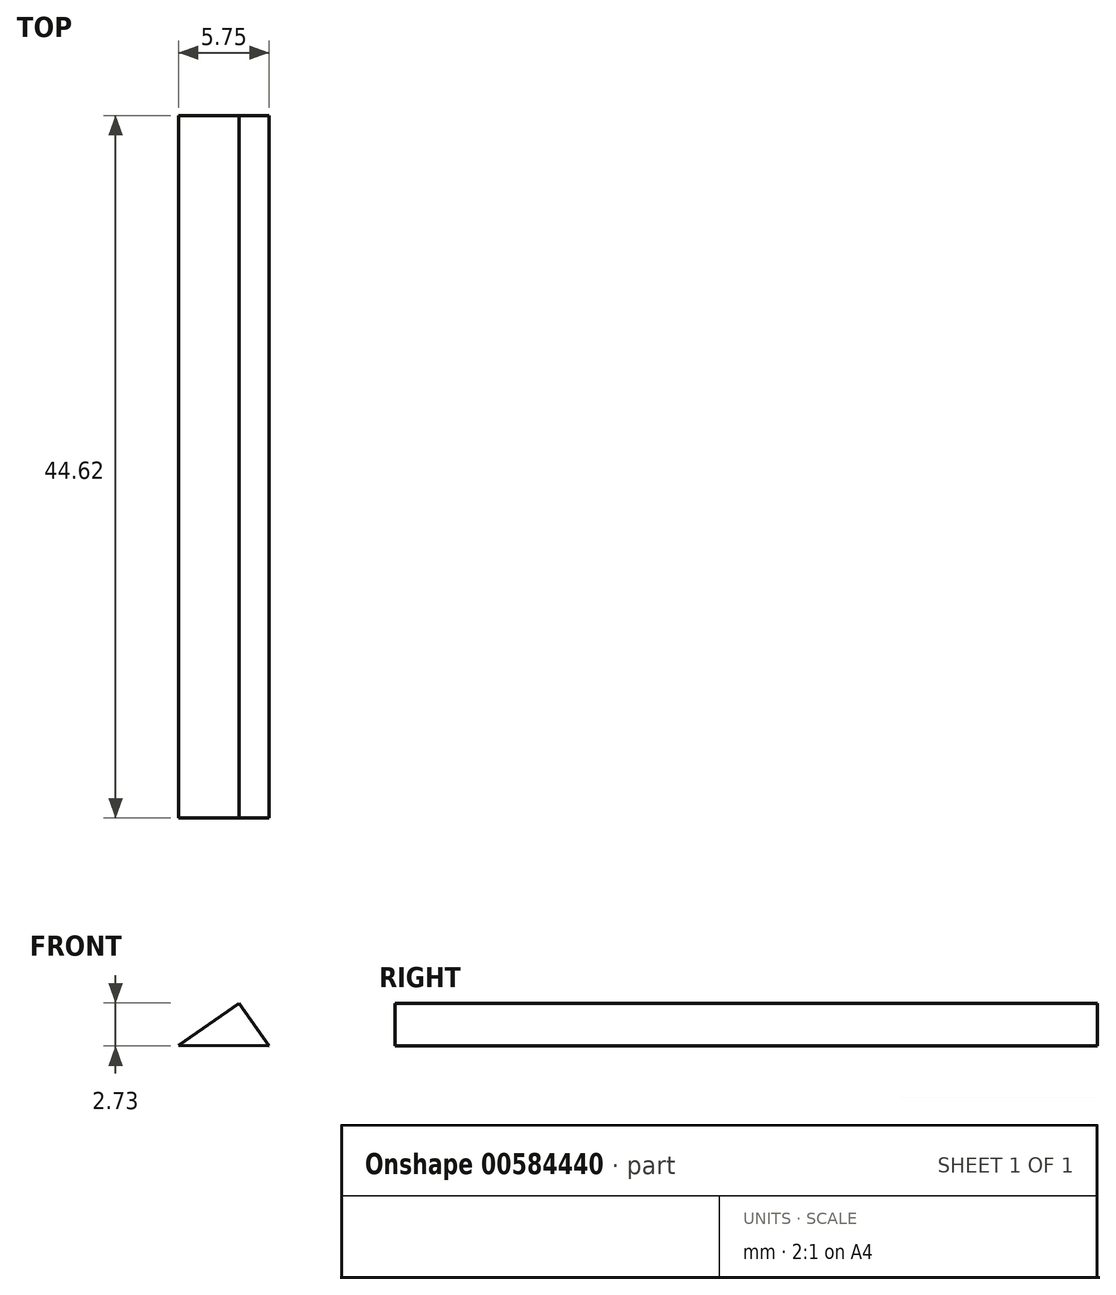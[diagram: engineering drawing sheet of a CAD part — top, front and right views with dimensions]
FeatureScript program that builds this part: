
annotation { "Feature Type Name" : "Feature", "Feature Type Description" : "" }
export const myFeature = defineFeature(function(context is Context, id is Id, definition is map)
    precondition{}
    {
        {
            var Q0;
            Q0=qCreatedBy(makeId("Front.planeOp"),FACE);
            var sketch = newSketch(context, id + "F0", { "sketchPlane" : qUnion([Q0])});
            skLineSegment(sketch, "E0", {"start": v(-47.67, 7.16) * mm, "end": v(-43.82, 9.86) * mm});
            skLineSegment(sketch, "E1", {"start": v(-43.82, 9.86) * mm, "end": v(-41.92, 7.13) * mm});
            skLineSegment(sketch, "E2", {"start": v(-47.67, 7.16) * mm, "end": v(-41.92, 7.13) * mm});
            skSolve(sketch);
        }
        {
            var Q0;
            Q0 = qSketchRegion(id + "F0", true);
            extrude(context, id + "F1", {"entities" : qUnion([Q0]), "depth" : 44.62 * mm, "offsetDistance" : 25 * mm});
        }
    });
